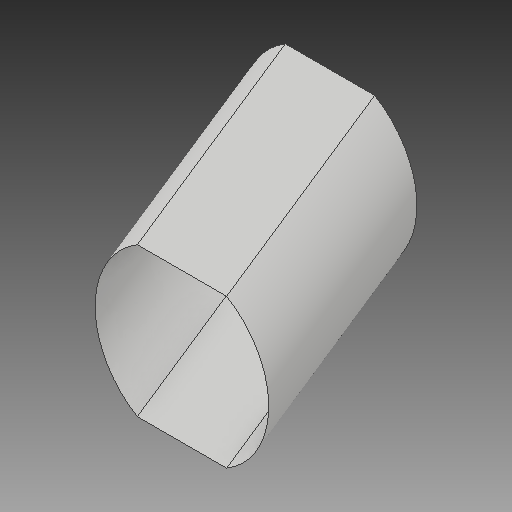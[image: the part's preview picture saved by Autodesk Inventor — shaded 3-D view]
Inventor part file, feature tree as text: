
AUTODESK INVENTOR PART (.ipt)
format: ipt  version: 2017 (Build 210142000, 142)  size: 114,176 bytes
history: native  units: in
note: dims shown in document units (in); Inventor stores cm internally (conversion verified against a paired STEP export)
features: sketch x2, plane x1, sweep x1, delete_face x1
ambient origin geometry x8: Origin, YZ Plane, XZ Plane, XY Plane, X Axis, Y Axis, Z Axis, Center Point
bodies: Solid1 (feature_tree)
feature tree (5):
  sketch  "Sketch1"  dims[d28=8.0in d30=0.0in d31=0.0in]
  plane  "Work Plane2"
  sweep  "ramp"
  delete_face  "Delete Face1"
  sketch  "Sketch6"  dims[d59=3.3333in d61=3.3333in d62=0.8521in d63=4.0in d65=3.8873in d66=3.8873in d70=1.6458in d76=3.3333in]
